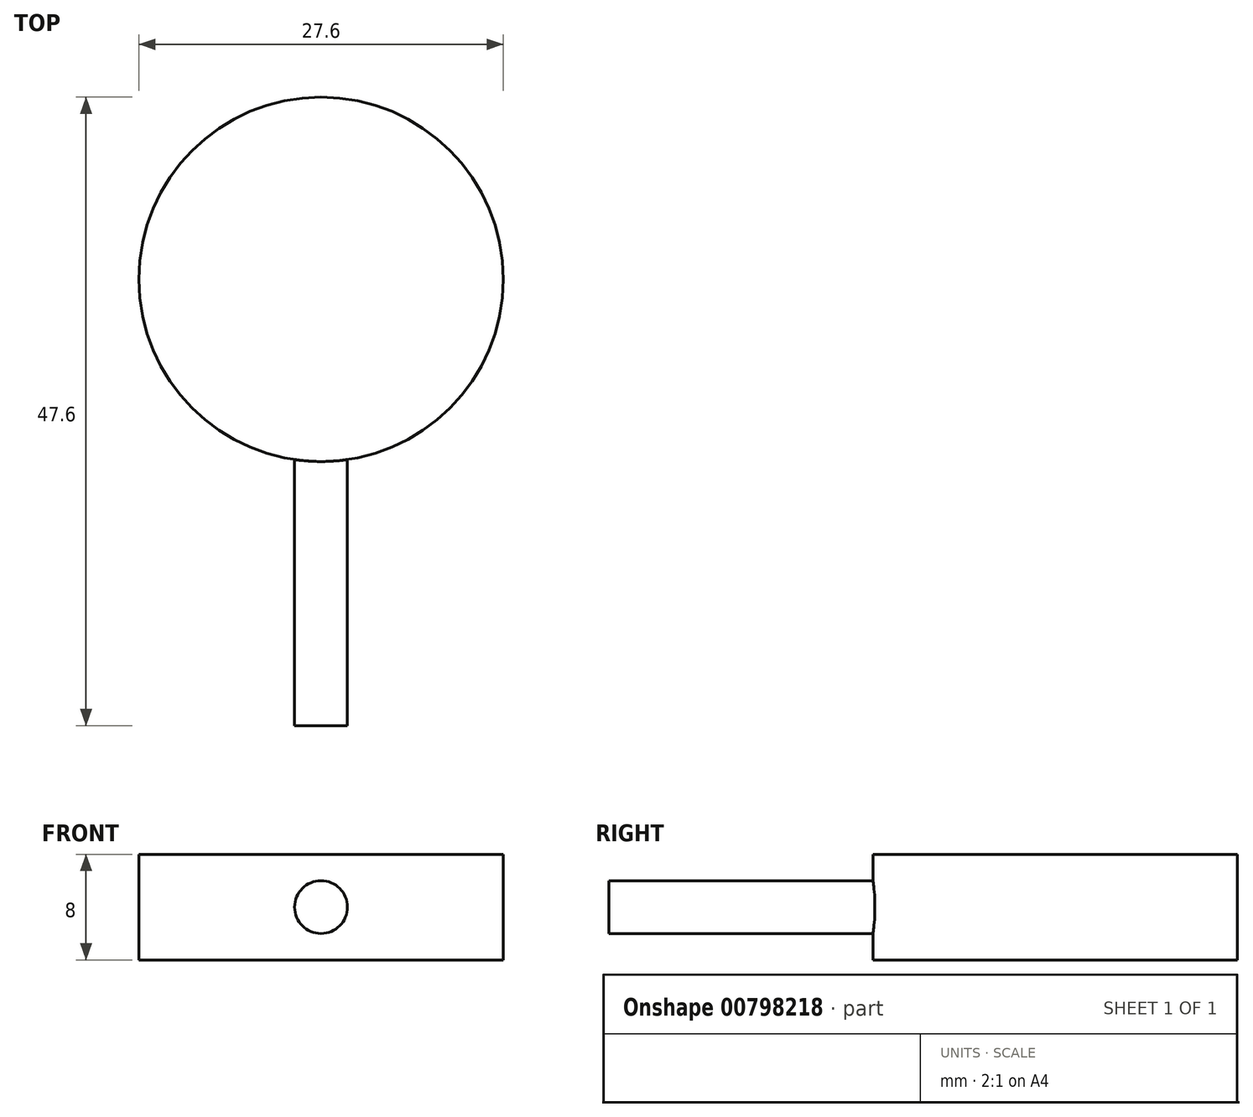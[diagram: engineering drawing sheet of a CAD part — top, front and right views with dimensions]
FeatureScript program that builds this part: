
annotation { "Feature Type Name" : "Feature", "Feature Type Description" : "" }
export const myFeature = defineFeature(function(context is Context, id is Id, definition is map)
    precondition{}
    {
        {
            var Q0;
            Q0=qCreatedBy(makeId("Top.planeOp"),FACE);
            var sketch = newSketch(context, id + "F0", { "sketchPlane" : qUnion([Q0])});
            skCircle(sketch, "E0", {"center": v(0, 0) * mm, "radius": 13.8 * mm});
            skSolve(sketch);
        }
        {
            var Q0;
            Q0=makeQuery(id+"F0.imprint","IMPRINT",FACE,{"disambiguationData":[TD([[makeQuery(id+"F0.imprint","IMPRINT",EDGE,{"derivedFrom":sQuery(id+"F0.wireOp",EDGE,"E0")}),1.0]])]});
            extrude(context, id + "F1", {"entities" : qUnion([Q0]), "depth" : 8 * mm, "offsetDistance" : 25 * mm});
        }
        {
            var Q0;
            Q0=qCreatedBy(makeId("Right.planeOp"),FACE);
            var sketch = newSketch(context, id + "F2", { "sketchPlane" : qUnion([Q0])});
            skLineSegment(sketch, "E1", {"start": v(-13.8, 0) * mm, "end": v(-13.8, 8) * mm});
            skSolve(sketch);
        }
        {
            var Q0;
            Q0=sQuery(id+"F2.wireOp",EDGE,"E1");
            cPoint(context, id + "F3", {"entities" : qUnion([Q0]), "parameter" : 0.5});
        }
        {
            var Q0;
            Q0=qCreatedBy(makeId("Front.planeOp"),FACE);
            var Q1;
            Q1 = qCreatedBy(id + "F3" ,VERTEX);
            cPlane(context, id + "F4", {"entities" : qUnion([Q0, Q1]), "cplaneType" : CPlaneType.PLANE_POINT, "offset" : 25 * mm, "width" : 150 * mm, "height" : 150 * mm});
        }
        {
            var Q0;
            Q0=qCreatedBy(id+"F4.planeOp",FACE);
            var sketch = newSketch(context, id + "F5", { "sketchPlane" : qUnion([Q0])});
            skPoint(sketch, "E2.0", {"position": v(0, 4) * mm});
            skCircle(sketch, "E3", {"center": v(0, 4) * mm, "radius": 2 * mm});
            skSolve(sketch);
        }
        {
            var Q0;
            Q0=makeQuery(id+"F5.imprint","IMPRINT",FACE,{"disambiguationData":[TD([[makeQuery(id+"F5.imprint","IMPRINT",EDGE,{"derivedFrom":sQuery(id+"F5.wireOp",EDGE,"E3")}),1.0]])]});
            var Q1;
            Q1=sQuery(id+"F5.wireOp",EDGE,"E3");
            extrude(context, id + "F6", {"entities" : qUnion([Q0]), "operationType" : NewBodyOperationType.ADD, "surfaceEntities" : qUnion([Q1]), "depth" : 20 * mm, "offsetDistance" : 25 * mm, "hasSecondDirection" : true, "secondDirectionOppositeDirection" : true, "secondDirectionDepth" : 13.7 * mm});
        }
    });
